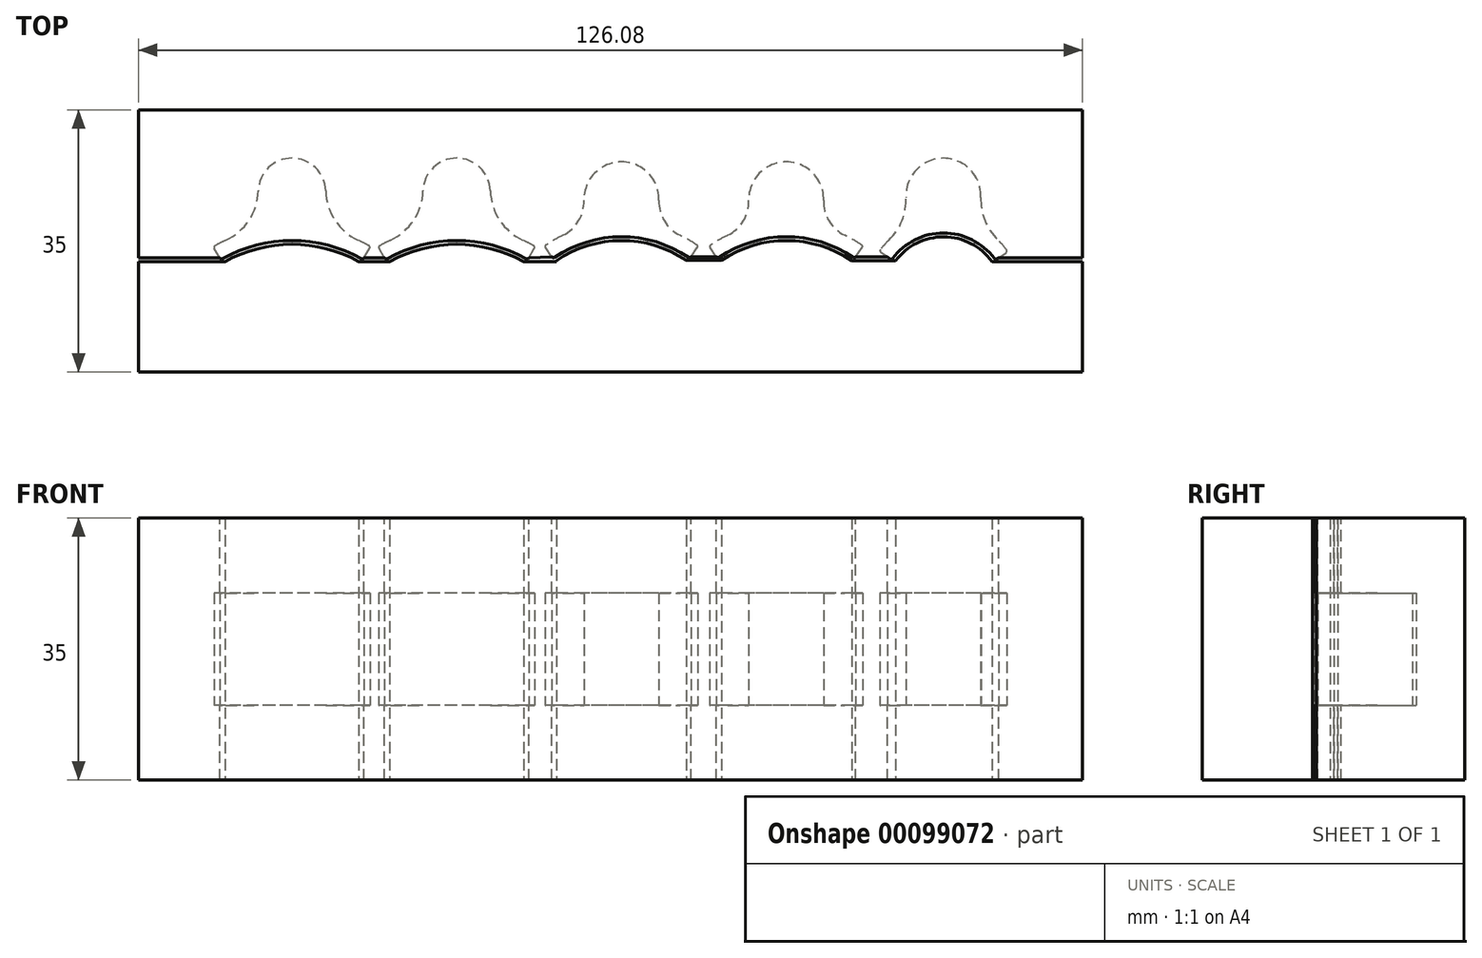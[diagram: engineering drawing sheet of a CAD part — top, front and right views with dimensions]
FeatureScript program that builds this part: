
annotation { "Feature Type Name" : "Feature", "Feature Type Description" : "" }
export const myFeature = defineFeature(function(context is Context, id is Id, definition is map)
    precondition{}
    {
        {
            var Q0;
            Q0=qCreatedBy(makeId("Top.planeOp"),FACE);
            var sketch = newSketch(context, id + "F0", { "sketchPlane" : qUnion([Q0])});
            skArc(sketch, "E0", {"start": v(9.29, -5.5) * mm, "mid": v(0, -3.07) * mm, "end": v(-9.29, -5.5) * mm});
            skArc(sketch, "E1", {"start": v(4.5, 3.56) * mm, "mid": v(0, 7.93) * mm, "end": v(-4.5, 3.56) * mm});
            skArc(sketch, "E2.0", {"start": v(10.28, -3.76) * mm, "mid": v(9.57, -3.38) * mm, "end": v(8.84, -3.02) * mm});
            skArc(sketch, "E3", {"start": v(-8.84, -3.02) * mm, "mid": v(-5.73, -0.35) * mm, "end": v(-4.5, 3.56) * mm});
            skArc(sketch, "E4", {"start": v(4.5, 3.56) * mm, "mid": v(5.73, -0.35) * mm, "end": v(8.84, -3.02) * mm});
            skLineSegment(sketch, "E5", {"start": v(9.62, -5.4) * mm, "end": v(10.37, -4.1) * mm});
            skLineSegment(sketch, "E6", {"start": v(-9.62, -5.4) * mm, "end": v(-10.37, -4.1) * mm});
            skArc(sketch, "E7.trimOffspring", {"start": v(-8.84, -3.02) * mm, "mid": v(-9.57, -3.38) * mm, "end": v(-10.28, -3.76) * mm});
            skPoint(sketch, "E8.visualSharp", {"position": v(9.5, -5.62) * mm});
            skArc(sketch, "E8.filletArc", {"start": v(9.29, -5.5) * mm, "mid": v(9.47, -5.52) * mm, "end": v(9.62, -5.4) * mm});
            skPoint(sketch, "E9.visualSharp", {"position": v(10.5, -3.88) * mm});
            skArc(sketch, "E9.filletArc", {"start": v(10.37, -4.1) * mm, "mid": v(10.4, -3.91) * mm, "end": v(10.28, -3.76) * mm});
            skPoint(sketch, "E10.visualSharp", {"position": v(-10.5, -3.88) * mm});
            skArc(sketch, "E10.filletArc", {"start": v(-10.28, -3.76) * mm, "mid": v(-10.4, -3.91) * mm, "end": v(-10.37, -4.1) * mm});
            skPoint(sketch, "E11.visualSharp", {"position": v(-9.5, -5.62) * mm});
            skArc(sketch, "E11.filletArc", {"start": v(-9.62, -5.4) * mm, "mid": v(-9.47, -5.52) * mm, "end": v(-9.29, -5.5) * mm});
            skPoint(sketch, "E12.1.0.7", {"position": v(10, -4) * mm});
            skArc(sketch, "E13.1.0.0", {"start": v(26.5, 3.56) * mm, "mid": v(27.73, -0.35) * mm, "end": v(30.84, -3.02) * mm});
            skPoint(sketch, "E13.1.0.1", {"position": v(32, -4) * mm});
            skArc(sketch, "E13.1.0.2", {"start": v(31.29, -5.5) * mm, "mid": v(22, -3.07) * mm, "end": v(12.71, -5.5) * mm});
            skArc(sketch, "E13.1.0.3", {"start": v(26.5, 3.56) * mm, "mid": v(22, 7.93) * mm, "end": v(17.5, 3.56) * mm});
            skPoint(sketch, "E13.1.0.4", {"position": v(12.5, -5.62) * mm});
            skPoint(sketch, "E13.1.0.5", {"position": v(32.5, -3.88) * mm});
            skArc(sketch, "E13.1.0.6", {"start": v(13.16, -3.02) * mm, "mid": v(16.27, -0.35) * mm, "end": v(17.5, 3.56) * mm});
            skPoint(sketch, "E13.1.0.7", {"position": v(31.5, -5.62) * mm});
            skPoint(sketch, "E13.1.0.8", {"position": v(11.5, -3.88) * mm});
            skArc(sketch, "E13.1.0.9", {"start": v(32.28, -3.76) * mm, "mid": v(31.57, -3.38) * mm, "end": v(30.84, -3.02) * mm});
            skArc(sketch, "E13.1.0.10", {"start": v(13.16, -3.02) * mm, "mid": v(12.43, -3.38) * mm, "end": v(11.72, -3.76) * mm});
            skArc(sketch, "E13.1.0.11", {"start": v(12.38, -5.4) * mm, "mid": v(12.53, -5.52) * mm, "end": v(12.71, -5.5) * mm});
            skArc(sketch, "E13.1.0.12", {"start": v(32.37, -4.1) * mm, "mid": v(32.4, -3.91) * mm, "end": v(32.28, -3.76) * mm});
            skArc(sketch, "E13.1.0.13", {"start": v(31.29, -5.5) * mm, "mid": v(31.47, -5.52) * mm, "end": v(31.62, -5.4) * mm});
            skArc(sketch, "E13.1.0.14", {"start": v(11.72, -3.76) * mm, "mid": v(11.6, -3.91) * mm, "end": v(11.63, -4.1) * mm});
            skLineSegment(sketch, "E13.1.0.15", {"start": v(31.62, -5.4) * mm, "end": v(32.37, -4.1) * mm});
            skLineSegment(sketch, "E13.1.0.16", {"start": v(12.38, -5.4) * mm, "end": v(11.63, -4.1) * mm});
            skLineSegment(sketch, "E13.direction1", {"start": v(0, -22.07) * mm, "end": v(22, -22.07) * mm, "construction": true});
            skArc(sketch, "E14", {"start": v(52.95, -5.3) * mm, "mid": v(44, -2.57) * mm, "end": v(35.05, -5.3) * mm});
            skArc(sketch, "E15", {"start": v(49, 2.29) * mm, "mid": v(44, 7.43) * mm, "end": v(39, 2.29) * mm});
            skArc(sketch, "E16.0", {"start": v(54.09, -3.66) * mm, "mid": v(52.98, -2.97) * mm, "end": v(51.82, -2.36) * mm});
            skArc(sketch, "E17", {"start": v(36.18, -2.36) * mm, "mid": v(38.28, -0.45) * mm, "end": v(39, 2.29) * mm});
            skArc(sketch, "E18", {"start": v(49, 2.29) * mm, "mid": v(49.72, -0.45) * mm, "end": v(51.82, -2.36) * mm});
            skLineSegment(sketch, "E19", {"start": v(53.3, -5.24) * mm, "end": v(54.15, -4.01) * mm});
            skLineSegment(sketch, "E20", {"start": v(34.7, -5.25) * mm, "end": v(33.85, -4.02) * mm});
            skArc(sketch, "E21.trimOffspring", {"start": v(36.18, -2.36) * mm, "mid": v(35.02, -2.97) * mm, "end": v(33.91, -3.67) * mm});
            skPoint(sketch, "E22.visualSharp", {"position": v(53.15, -5.45) * mm});
            skArc(sketch, "E22.filletArc", {"start": v(52.95, -5.3) * mm, "mid": v(53.13, -5.35) * mm, "end": v(53.3, -5.24) * mm});
            skPoint(sketch, "E23.visualSharp", {"position": v(54.3, -3.8) * mm});
            skArc(sketch, "E23.filletArc", {"start": v(54.15, -4.01) * mm, "mid": v(54.2, -3.82) * mm, "end": v(54.09, -3.66) * mm});
            skPoint(sketch, "E24.visualSharp", {"position": v(33.7, -3.8) * mm});
            skArc(sketch, "E24.filletArc", {"start": v(33.91, -3.67) * mm, "mid": v(33.8, -3.83) * mm, "end": v(33.85, -4.02) * mm});
            skPoint(sketch, "E25.visualSharp", {"position": v(34.85, -5.45) * mm});
            skArc(sketch, "E25.filletArc", {"start": v(34.7, -5.25) * mm, "mid": v(34.86, -5.35) * mm, "end": v(35.05, -5.3) * mm});
            skPoint(sketch, "E26.1.0.7", {"position": v(53.98, -3.92) * mm});
            skPoint(sketch, "E27.1.0.8", {"position": v(55.48, -3.05) * mm});
            skPoint(sketch, "E28.1.0.0", {"position": v(55.7, -3.8) * mm});
            skArc(sketch, "E28.1.0.1", {"start": v(58.18, -2.36) * mm, "mid": v(60.28, -0.45) * mm, "end": v(61, 2.29) * mm});
            skArc(sketch, "E28.1.0.2", {"start": v(71, 2.29) * mm, "mid": v(66, 7.43) * mm, "end": v(61, 2.29) * mm});
            skPoint(sketch, "E28.1.0.3", {"position": v(56.85, -5.45) * mm});
            skArc(sketch, "E28.1.0.4", {"start": v(56.7, -5.25) * mm, "mid": v(56.86, -5.35) * mm, "end": v(57.05, -5.3) * mm});
            skPoint(sketch, "E28.1.0.5", {"position": v(77.48, -3.05) * mm});
            skArc(sketch, "E28.1.0.6", {"start": v(71, 2.29) * mm, "mid": v(71.72, -0.45) * mm, "end": v(73.82, -2.36) * mm});
            skPoint(sketch, "E28.1.0.7", {"position": v(75.98, -3.92) * mm});
            skArc(sketch, "E28.1.0.8", {"start": v(76.09, -3.66) * mm, "mid": v(74.98, -2.97) * mm, "end": v(73.82, -2.36) * mm});
            skPoint(sketch, "E28.1.0.9", {"position": v(76.3, -3.8) * mm});
            skArc(sketch, "E28.1.0.10", {"start": v(74.95, -5.3) * mm, "mid": v(66, -2.57) * mm, "end": v(57.05, -5.3) * mm});
            skArc(sketch, "E28.1.0.11", {"start": v(58.18, -2.36) * mm, "mid": v(57.02, -2.97) * mm, "end": v(55.91, -3.67) * mm});
            skPoint(sketch, "E28.1.0.12", {"position": v(75.15, -5.45) * mm});
            skLineSegment(sketch, "E28.1.0.13", {"start": v(56.7, -5.25) * mm, "end": v(55.85, -4.02) * mm});
            skLineSegment(sketch, "E28.1.0.14", {"start": v(75.3, -5.24) * mm, "end": v(76.15, -4.01) * mm});
            skArc(sketch, "E28.1.0.15", {"start": v(74.95, -5.3) * mm, "mid": v(75.13, -5.35) * mm, "end": v(75.3, -5.24) * mm});
            skArc(sketch, "E28.1.0.16", {"start": v(76.15, -4.01) * mm, "mid": v(76.2, -3.82) * mm, "end": v(76.09, -3.66) * mm});
            skLineSegment(sketch, "E28.direction1", {"start": v(44, -18.57) * mm, "end": v(66, -18.57) * mm, "construction": true});
            skPoint(sketch, "E29.newPointA", {"position": v(55.85, -4.02) * mm});
            skPoint(sketch, "E29.newPointB", {"position": v(55.91, -3.67) * mm});
            skArc(sketch, "E29.filletArc", {"start": v(55.91, -3.67) * mm, "mid": v(55.8, -3.83) * mm, "end": v(55.85, -4.02) * mm});
            skArc(sketch, "E30", {"start": v(93.8, -5.47) * mm, "mid": v(87, -2.07) * mm, "end": v(80.2, -5.47) * mm});
            skArc(sketch, "E31", {"start": v(92, 2.71) * mm, "mid": v(87, 7.93) * mm, "end": v(82, 2.71) * mm});
            skArc(sketch, "E32.0", {"start": v(95.43, -4.3) * mm, "mid": v(94.88, -3.63) * mm, "end": v(94.28, -3) * mm});
            skArc(sketch, "E33", {"start": v(79.72, -3) * mm, "mid": v(81.48, -0.4) * mm, "end": v(82, 2.71) * mm});
            skArc(sketch, "E34", {"start": v(92, 2.71) * mm, "mid": v(92.52, -0.4) * mm, "end": v(94.28, -3) * mm});
            skLineSegment(sketch, "E35", {"start": v(94.14, -5.52) * mm, "end": v(95.37, -4.66) * mm});
            skLineSegment(sketch, "E36", {"start": v(79.86, -5.52) * mm, "end": v(78.64, -4.65) * mm});
            skArc(sketch, "E37.trimOffspring", {"start": v(79.72, -3) * mm, "mid": v(79.12, -3.63) * mm, "end": v(78.58, -4.3) * mm});
            skPoint(sketch, "E38.visualSharp", {"position": v(93.94, -5.67) * mm});
            skArc(sketch, "E38.filletArc", {"start": v(93.8, -5.47) * mm, "mid": v(93.96, -5.57) * mm, "end": v(94.14, -5.52) * mm});
            skPoint(sketch, "E39.visualSharp", {"position": v(95.58, -4.51) * mm});
            skArc(sketch, "E39.filletArc", {"start": v(95.37, -4.66) * mm, "mid": v(95.47, -4.5) * mm, "end": v(95.43, -4.3) * mm});
            skPoint(sketch, "E40.visualSharp", {"position": v(78.43, -4.5) * mm});
            skArc(sketch, "E40.filletArc", {"start": v(78.58, -4.3) * mm, "mid": v(78.53, -4.49) * mm, "end": v(78.64, -4.65) * mm});
            skPoint(sketch, "E41.visualSharp", {"position": v(80.06, -5.66) * mm});
            skArc(sketch, "E41.filletArc", {"start": v(79.86, -5.52) * mm, "mid": v(80.04, -5.56) * mm, "end": v(80.2, -5.47) * mm});
            skPoint(sketch, "E42.1.0.7", {"position": v(99.15, -4.45) * mm});
            skPoint(sketch, "E43.1.0.8", {"position": v(100.65, -3.58) * mm});
            skArc(sketch, "E44.0", {"start": v(8.94, -5.88) * mm, "mid": v(0, -3.57) * mm, "end": v(-8.94, -5.88) * mm});
            skArc(sketch, "E45.0", {"start": v(30.94, -5.88) * mm, "mid": v(22, -3.57) * mm, "end": v(13.06, -5.88) * mm});
            skArc(sketch, "E46.0", {"start": v(52.67, -5.72) * mm, "mid": v(43.98, -3.07) * mm, "end": v(35.3, -5.74) * mm});
            skArc(sketch, "E47.0", {"start": v(74.75, -5.78) * mm, "mid": v(66.05, -3.07) * mm, "end": v(57.33, -5.72) * mm});
            skArc(sketch, "E48.0", {"start": v(93.48, -5.88) * mm, "mid": v(87.06, -2.57) * mm, "end": v(80.6, -5.78) * mm});
            skLineSegment(sketch, "E49", {"start": v(-31.34, -5.88) * mm, "end": v(-8.94, -5.88) * mm});
            skLineSegment(sketch, "E50", {"start": v(8.94, -5.88) * mm, "end": v(13.06, -5.88) * mm});
            skLineSegment(sketch, "E51", {"start": v(30.94, -5.88) * mm, "end": v(35.3, -5.88) * mm});
            skLineSegment(sketch, "E52", {"start": v(35.3, -5.88) * mm, "end": v(35.3, -5.74) * mm});
            skLineSegment(sketch, "E53", {"start": v(52.67, -5.72) * mm, "end": v(57.33, -5.72) * mm});
            skLineSegment(sketch, "E54", {"start": v(93.48, -5.88) * mm, "end": v(106.78, -5.88) * mm});
            skLineSegment(sketch, "E55", {"start": v(74.75, -5.78) * mm, "end": v(80.6, -5.78) * mm});
            skLineSegment(sketch, "E56.trimOffspring", {"start": v(75.27, -5.28) * mm, "end": v(79.52, -5.28) * mm});
            skLineSegment(sketch, "E57.0", {"start": v(94.35, -5.38) * mm, "end": v(106.78, -5.38) * mm});
            skLineSegment(sketch, "E58", {"start": v(106.78, -5.38) * mm, "end": v(106.78, -5.88) * mm});
            skLineSegment(sketch, "E59.0", {"start": v(53.3, -5.22) * mm, "end": v(56.69, -5.22) * mm});
            skLineSegment(sketch, "E60.0", {"start": v(9.64, -5.38) * mm, "end": v(12.36, -5.38) * mm});
            skLineSegment(sketch, "E61.0", {"start": v(-31.34, -5.38) * mm, "end": v(-9.64, -5.38) * mm});
            skLineSegment(sketch, "E62", {"start": v(-31.34, -5.38) * mm, "end": v(-31.34, -5.88) * mm});
            skLineSegment(sketch, "E63.trimOffspring", {"start": v(31.64, -5.38) * mm, "end": v(34.71, -5.26) * mm});
            skSolve(sketch);
        }
        {
            var Q0;
            Q0=qCreatedBy(makeId("Top.planeOp"),FACE);
            var sketch = newSketch(context, id + "F1", { "sketchPlane" : qUnion([Q0])});
            skLineSegment(sketch, "E64.bottom", {"start": v(-20.5, -20.62) * mm, "end": v(105.58, -20.62) * mm});
            skLineSegment(sketch, "E64.top", {"start": v(-20.5, 14.38) * mm, "end": v(105.58, 14.38) * mm});
            skLineSegment(sketch, "E64.left", {"start": v(-20.5, -20.62) * mm, "end": v(-20.5, 14.38) * mm});
            skLineSegment(sketch, "E64.right", {"start": v(105.58, -20.62) * mm, "end": v(105.58, 14.38) * mm});
            skSolve(sketch);
        }
        {
            var Q0;
            Q0 = qSketchRegion(id + "F1", true);
            extrude(context, id + "F2", {"entities" : qUnion([Q0]), "depth" : 25 * mm});
        }
        {
            var Q0;
            Q0 = qSketchRegion(id + "F1", true);
            extrude(context, id + "F3", {"entities" : qUnion([Q0]), "operationType" : NewBodyOperationType.ADD, "oppositeDirection" : true, "depth" : 10 * mm});
        }
        {
            var Q0;
            Q0 = qSketchRegion(id + "F0", true);
            extrude(context, id + "F4", {"entities" : qUnion([Q0]), "operationType" : NewBodyOperationType.REMOVE, "depth" : 15 * mm});
        }
        {
            var Q0;
            Q0=makeQuery(id+"F0.imprint","IMPRINT",FACE,{"disambiguationData":[TD([[makeQuery(id+"F0.imprint","IMPRINT",EDGE,{"derivedFrom":sQuery(id+"F0.wireOp",EDGE,"E0")}),1.0]])]});
            extrude(context, id + "F5", {"entities" : qUnion([Q0]), "operationType" : NewBodyOperationType.REMOVE, "endBound" : BoundingType.SYMMETRIC, "oppositeDirection" : true, "depth" : 60 * mm});
        }
    });
